# Revit family: NBS_ConceptCubicleSystems_DuctAndWlPnlLngSystms_MediForm
name_source: partatom
category: Furniture
units: mm (PartAtom-declared; Revit-internal decimal feet)

## family parameters
Always vertical = Yes
Cut with Voids When Loaded = No
Room Calculation Point = No
Shared = No
Work Plane-Based = No

## types (1)
- MediForm
    AccessPanelDoorMaterial = NBS_ConceptCubicleSystems_PVCCladding_SatinLRV93
    AssetType = Fixed
    BIMObjectName = NBS_ConceptCubicleSystems_DuctAndWallPanelLiningSystems_MediForm
    Category = Ss_25_25_45_25:Duct and wall panel lining systems
    Color = Black,Blue,Cream,Green,Grey,Orange,Pink,Purple,Red,White,Yellow
    ColourFinish = Cotton LRV 81,Gloss LRV 93,Satin LRV 93,Antimicrobial Sterling LRV 93,Orange LRV 17,Green LRV 47,Lime Green LRV 60,Pastel Cream LRV 88,Mushroom LRV 39,Pastel Grey LRV 81,Dove LRV 88,Black LRV 1,Mid Grey LRV 11,Marine Blue LRV 34,Blue LRV 30,Racing Green LRV 34,Yellow LRV 80,Satin White,Red LRV 3,Pink LRV 13,Purple LRV 1,Pacific Blue LRV 8,Teal LRV 10,Turquoise LRV 33,Avocado LRV 34,Duck Egg LRV 78,Pastel Green LRV 75,Peppermint LRV 61,Pastel Blue LRV 64,Goose Grey LRV 29
    Description = A prefabricated, modular wall panel system complete with sanitaryware
    DurationUnit = year
    Fasteners = Brackets to wall
    Finish = Satin,Gloss
    IfcExportAs = IfcFurnitureType
    IfcExportType = USERDEFINED
    ManufacturerName = Concept Cubicle Systems
    ManufacturerURL = www.conceptcubiclesystems.co.uk
    Material = Polyvinyl chloride (PVC)
    ModelReference = MediForm
    NBSCertification = www.nationalbimlibrary.com/cert/fmsvawtm
    Name = DuctAndWallPanelLiningSystems_MediForm_ConceptCubicleSystems
    NominalLength = 0 mm  [stored 0 ft]
    NonintegralFinishes = Rebated flush access door detail
    PanelThickness = 22 mm
    Panels = Anti-microbial PVC - wall to wall,Anti-microbial PVC - corner,Anti-microbial PVC - standalone
    ProductInformation = https://www.conceptcubiclesystems.co.uk
    Shape = Other
    Size = Bespoke
    SustainabilityPerformance = n/a,
    SystemAccessories = Heavy duty hinges,Locks,Not required
    Uniclass2015Code = Ss_25_25_45_25
    Uniclass2015Title = Duct and wall panel lining systems
    Uniclass2015Version = Systems v1.22
    Version = 2
    WallPanelMaterial = NBS_ConceptCubicleSystems_PVCCladding_SatinLRV93
    WarrantyDurationUnit = year

note: [stored X ft] marks values corroborated as IEEE doubles in the binary element streams (Revit-internal decimal feet)

## geometry (parser evidence)
native form markers: Sweep x4
no freeform markers — native parametric forms only
